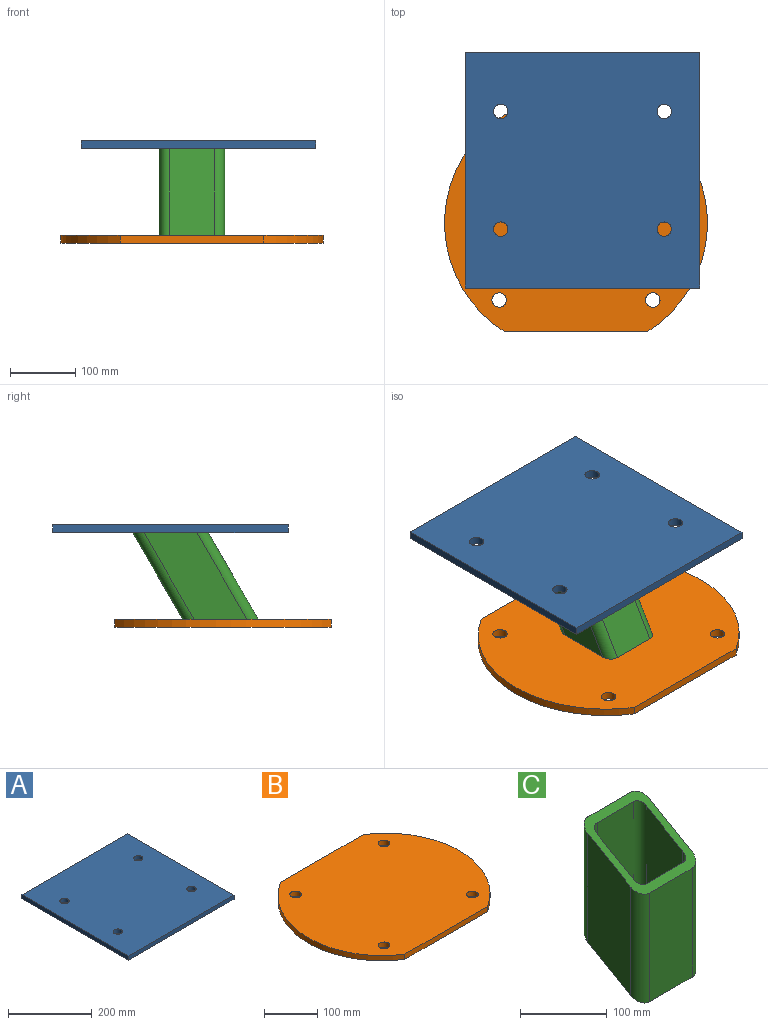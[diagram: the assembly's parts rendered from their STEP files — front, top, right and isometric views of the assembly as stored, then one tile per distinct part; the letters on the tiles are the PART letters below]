
ASSEMBLY  parts=3 mates=2
PART A: 10 faces, bbox 358x360x12 mm
  f0: plane 358x12mm, normal (0,1,0), area 4296mm2, adj f1,f6,f8,f9
  f1: plane 360x12mm, normal (-1,0,0), area 4320mm2, adj f0,f2,f8,f9
  f2: plane 358x12mm, normal (0,-1,0), area 4296mm2, adj f1,f6,f8,f9
  f3: cylinder r=11mm len=22mm, axis (0,0,-1), area 829.4mm2, adj f8,f9
  f4: cylinder r=11mm len=22mm, axis (0,0,-1), area 829.4mm2, adj f8,f9
  f5: cylinder r=11mm len=22mm, axis (0,0,-1), area 829.4mm2, adj f8,f9
  f6: plane 360x12mm, normal (1,0,0), area 4320mm2, adj f0,f2,f8,f9
  f7: cylinder r=11mm len=22mm, axis (0,0,-1), area 829.4mm2, adj f8,f9
  f8: plane 360x358mm, normal (0,0,1), area 127359.5mm2, adj f0,f1,f2,f3,f4,f5,f6,f7
  f9: plane 360x358mm, normal (0,0,-1), area 127359.5mm2, adj f0,f1,f2,f3,f4,f5,f6,f7
PART B: 10 faces, bbox 402x331x12 mm
  f0: plane 220.01x12mm, normal (0,1,0), area 2640.2mm2, adj f1,f7,f8,f9
  f1: cylinder r=196mm len=331mm, axis (0,0,-1), area 4729.5mm2, adj f0,f2,f8,f9
  f2: plane 220x12mm, normal (0,-1,0), area 2640mm2, adj f1,f7,f8,f9
  f3: cylinder r=11mm len=22mm, axis (0,0,-1), area 829.4mm2, adj f8,f9
  f4: cylinder r=11mm len=22mm, axis (0,0,-1), area 829.4mm2, adj f8,f9
  f5: cylinder r=11mm len=22mm, axis (0,0,-1), area 829.4mm2, adj f8,f9
  f6: cylinder r=11mm len=22mm, axis (0,0,-1), area 829.4mm2, adj f8,f9
  f7: cylinder r=196mm len=331mm, axis (0,0,-1), area 4729.5mm2, adj f0,f2,f8,f9
  f8: plane 402x331mm, normal (0,0,1), area 113794.2mm2, adj f0,f1,f2,f3,f4,f5,f6,f7
  f9: plane 402x331mm, normal (0,0,-1), area 113794.2mm2, adj f0,f1,f2,f3,f4,f5,f6,f7
PART C: 18 faces, bbox 100x100x211.3 mm
  f0: cylinder r=15mm len=162.24mm, axis (0,0,-1), area 3618.5mm2, adj f6,f7,f8,f9
  f1: cylinder r=15mm len=162.24mm, axis (0,0,-1), area 3618.5mm2, adj f3,f7,f8,f9
  f2: cylinder r=15mm len=162.24mm, axis (0,0,-1), area 3618.5mm2, adj f3,f5,f8,f9
  f3: plane 193.99x70mm, normal (1,0,0), area 10750.3mm2, adj f1,f2,f8,f9
  f4: cylinder r=15mm len=162.24mm, axis (0,0,-1), area 3618.5mm2, adj f5,f6,f8,f9
  f5: plane 153.58x70mm, normal (0,-1,0), area 10750.3mm2, adj f2,f4,f8,f9
  f6: plane 193.99x70mm, normal (-1,0,0), area 10750.3mm2, adj f0,f4,f8,f9
  f7: plane 153.58x70mm, normal (0,1,0), area 10750.3mm2, adj f0,f1,f8,f9
  f8: plane 100x100mm, normal (0,0.5,-0.87), area 4033mm2, adj f0,f1,f2,f3,f4,f5,f6,f7
  f9: plane 100x100mm, normal (0,-0.5,0.87), area 4033mm2, adj f0,f1,f2,f3,f4,f5,f6,f7
  f10: cylinder r=10mm len=159.35mm, axis (0,0,-1), area 2412.4mm2, adj f8,f9,f11,f17
  f11: plane 153.58x60mm, normal (0,-1,0), area 9214.5mm2, adj f8,f9,f10,f12
  f12: cylinder r=10mm len=159.35mm, axis (0,0,-1), area 2412.4mm2, adj f8,f9,f11,f13
  f13: plane 188.22x60mm, normal (-1,0,0), area 9214.5mm2, adj f8,f9,f12,f14
  f14: cylinder r=10mm len=159.35mm, axis (0,0,-1), area 2412.4mm2, adj f8,f9,f13,f15
  f15: plane 153.58x60mm, normal (0,1,0), area 9214.5mm2, adj f8,f9,f14,f16
  f16: cylinder r=10mm len=159.35mm, axis (0,0,-1), area 2412.4mm2, adj f8,f9,f15,f17
  f17: plane 188.22x60mm, normal (1,0,0), area 9214.5mm2, adj f8,f9,f10,f16
PLACE A t=(-237.18,24.16,-96.1)mm fixed
PLACE B t=(-247.18,-56.44,-241.1)mm
PLACE C rot(axis=(-1,0,0),30deg) t=(-247.18,-73.91,-265.96)mm
MATE parallel C.f9 <-> A.f9  axis (0,0,1) through (-287.18,24.16,-96.1)mm
MATE parallel B.f8 <-> C.f8  axis (0,0,1) through (-247.18,-56.44,-229.1)mm
